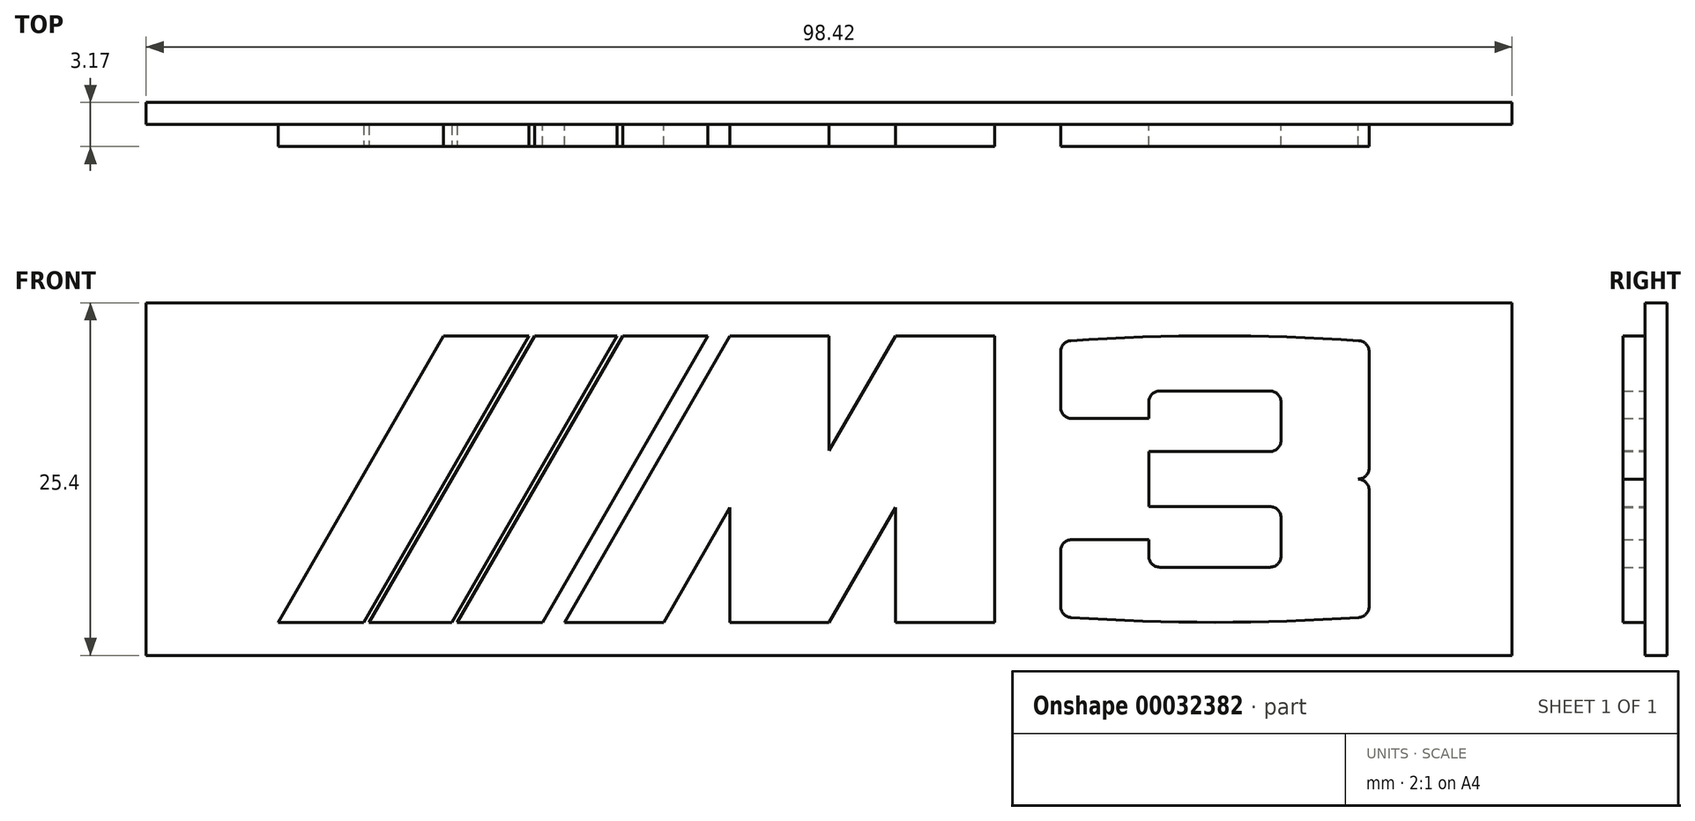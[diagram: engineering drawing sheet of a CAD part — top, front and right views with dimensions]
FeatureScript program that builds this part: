
annotation { "Feature Type Name" : "Feature", "Feature Type Description" : "" }
export const myFeature = defineFeature(function(context is Context, id is Id, definition is map)
    precondition{}
    {
        {
            var Q0;
            Q0=qCreatedBy(makeId("Front.planeOp"),FACE);
            var sketch = newSketch(context, id + "F0", { "sketchPlane" : qUnion([Q0])});
            skLineSegment(sketch, "E0.bottom", {"start": v(0, 0) * mm, "end": v(98.43, 0) * mm});
            skLineSegment(sketch, "E0.top", {"start": v(0, 25.4) * mm, "end": v(98.43, 25.4) * mm});
            skLineSegment(sketch, "E0.left", {"start": v(0, 0) * mm, "end": v(0, 25.4) * mm});
            skLineSegment(sketch, "E0.right", {"start": v(98.43, 0) * mm, "end": v(98.43, 25.4) * mm});
            skSolve(sketch);
        }
        {
            var Q0;
            Q0=makeQuery(id+"F0.imprint","IMPRINT",FACE,{"disambiguationData":[TD([[makeQuery(id+"F0.imprint","IMPRINT",EDGE,{"derivedFrom":sQuery(id+"F0.wireOp",EDGE,"E0.bottom")}),1.0]])]});
            extrude(context, id + "F1", {"entities" : qUnion([Q0]), "depth" : 1.59 * mm});
        }
        {
            var Q0;
            Q0=makeQuery(id+"F1.opExtrude","CAP_FACE",FACE,{"disambiguationData":[OSD([sQuery(id+"F0.wireOp",EDGE,"E0.bottom"),sQuery(id+"F0.wireOp",EDGE,"E0.top"),sQuery(id+"F0.wireOp",EDGE,"E0.left"),sQuery(id+"F0.wireOp",EDGE,"E0.right")])],"isStart":false});
            var sketch = newSketch(context, id + "F2", { "sketchPlane" : qUnion([Q0])});
            skLineSegment(sketch, "E1", {"start": v(0, 2.38) * mm, "end": v(98.43, 2.38) * mm, "construction": true});
            skLineSegment(sketch, "E2", {"start": v(0, 23.02) * mm, "end": v(98.43, 23.02) * mm, "construction": true});
            skLineSegment(sketch, "E3", {"start": v(9.53, 2.38) * mm, "end": v(21.44, 23.02) * mm});
            skLineSegment(sketch, "E4", {"start": v(21.44, 23.02) * mm, "end": v(40.5, 23.02) * mm});
            skLineSegment(sketch, "E5", {"start": v(40.5, 23.02) * mm, "end": v(28.58, 2.38) * mm});
            skLineSegment(sketch, "E6", {"start": v(28.58, 2.38) * mm, "end": v(9.53, 2.38) * mm});
            skLineSegment(sketch, "E7", {"start": v(30.16, 2.38) * mm, "end": v(42.08, 23.02) * mm});
            skLineSegment(sketch, "E8", {"start": v(42.08, 23.02) * mm, "end": v(49.22, 23.02) * mm});
            skLineSegment(sketch, "E9", {"start": v(49.22, 23.02) * mm, "end": v(49.22, 14.75) * mm});
            skLineSegment(sketch, "E10", {"start": v(49.22, 14.75) * mm, "end": v(54, 23.02) * mm});
            skLineSegment(sketch, "E11", {"start": v(54, 23.02) * mm, "end": v(61.14, 23.02) * mm});
            skLineSegment(sketch, "E12", {"start": v(61.14, 23.02) * mm, "end": v(61.14, 2.38) * mm});
            skLineSegment(sketch, "E13", {"start": v(61.14, 2.38) * mm, "end": v(54, 2.38) * mm});
            skLineSegment(sketch, "E14", {"start": v(54, 2.38) * mm, "end": v(54, 10.65) * mm});
            skLineSegment(sketch, "E15", {"start": v(54, 10.65) * mm, "end": v(49.22, 2.38) * mm});
            skLineSegment(sketch, "E16", {"start": v(49.22, 2.38) * mm, "end": v(42.08, 2.38) * mm});
            skLineSegment(sketch, "E17", {"start": v(42.08, 2.38) * mm, "end": v(42.08, 10.65) * mm});
            skLineSegment(sketch, "E18", {"start": v(42.08, 10.65) * mm, "end": v(37.3, 2.38) * mm});
            skLineSegment(sketch, "E19", {"start": v(37.3, 2.38) * mm, "end": v(30.16, 2.38) * mm});
            skLineSegment(sketch, "E20.left", {"start": v(65.9, 21.88) * mm, "end": v(65.9, 17.86) * mm});
            skLineSegment(sketch, "E20.right", {"start": v(88.12, 21.88) * mm, "end": v(88.12, 16.87) * mm});
            skPoint(sketch, "E21.visualSharp", {"position": v(65.9, 23.02) * mm});
            skPoint(sketch, "E22.visualSharp", {"position": v(65.9, 2.38) * mm});
            skPoint(sketch, "E23.visualSharp", {"position": v(88.12, 2.38) * mm});
            skLineSegment(sketch, "E24", {"start": v(87.33, 23.02) * mm, "end": v(87.33, 2.38) * mm, "construction": true});
            skPoint(sketch, "E25", {"position": v(87.33, 12.7) * mm});
            skArc(sketch, "E26", {"start": v(87.33, 12.7) * mm, "mid": v(87.9, 12.93) * mm, "end": v(88.12, 13.5) * mm});
            skArc(sketch, "E27", {"start": v(88.12, 11.9) * mm, "mid": v(87.9, 12.47) * mm, "end": v(87.33, 12.7) * mm});
            skLineSegment(sketch, "E28", {"start": v(65.9, 12.7) * mm, "end": v(88.12, 12.7) * mm, "construction": true});
            skLineSegment(sketch, "E29", {"start": v(66.7, 17.07) * mm, "end": v(72.25, 17.07) * mm});
            skLineSegment(sketch, "E30", {"start": v(66.7, 8.33) * mm, "end": v(72.25, 8.33) * mm});
            skLineSegment(sketch, "E31", {"start": v(72.25, 17.07) * mm, "end": v(72.25, 18.26) * mm});
            skLineSegment(sketch, "E32", {"start": v(73.04, 19.05) * mm, "end": v(80.98, 19.05) * mm});
            skLineSegment(sketch, "E33", {"start": v(81.77, 18.26) * mm, "end": v(81.77, 15.48) * mm});
            skLineSegment(sketch, "E34", {"start": v(80.98, 14.68) * mm, "end": v(72.25, 14.68) * mm});
            skLineSegment(sketch, "E35", {"start": v(72.25, 14.68) * mm, "end": v(72.25, 10.72) * mm});
            skLineSegment(sketch, "E36", {"start": v(72.25, 10.72) * mm, "end": v(80.98, 10.72) * mm});
            skLineSegment(sketch, "E37", {"start": v(81.77, 9.92) * mm, "end": v(81.77, 7.14) * mm});
            skLineSegment(sketch, "E38", {"start": v(80.98, 6.35) * mm, "end": v(73.04, 6.35) * mm});
            skLineSegment(sketch, "E39", {"start": v(72.25, 7.14) * mm, "end": v(72.25, 8.33) * mm});
            skLineSegment(sketch, "E40", {"start": v(81.77, 16.87) * mm, "end": v(88.12, 16.87) * mm, "construction": true});
            skLineSegment(sketch, "E41.trimOffspring", {"start": v(65.9, 7.54) * mm, "end": v(65.9, 3.52) * mm});
            skArc(sketch, "E42", {"start": v(66.64, 2.73) * mm, "mid": v(77.01, 2.38) * mm, "end": v(87.38, 2.73) * mm});
            skArc(sketch, "E43", {"start": v(87.38, 22.67) * mm, "mid": v(77.01, 23.02) * mm, "end": v(66.64, 22.67) * mm});
            skPoint(sketch, "E44.visualSharp", {"position": v(88.12, 22.62) * mm});
            skArc(sketch, "E44.filletArc", {"start": v(88.12, 21.88) * mm, "mid": v(87.9, 22.42) * mm, "end": v(87.38, 22.67) * mm});
            skPoint(sketch, "E45.visualSharp", {"position": v(65.9, 22.62) * mm});
            skArc(sketch, "E45.filletArc", {"start": v(66.64, 22.67) * mm, "mid": v(66.11, 22.42) * mm, "end": v(65.9, 21.88) * mm});
            skPoint(sketch, "E46.visualSharp", {"position": v(65.9, 17.07) * mm});
            skArc(sketch, "E46.filletArc", {"start": v(65.9, 17.86) * mm, "mid": v(66.13, 17.3) * mm, "end": v(66.7, 17.07) * mm});
            skPoint(sketch, "E47.visualSharp", {"position": v(65.9, 8.33) * mm});
            skArc(sketch, "E47.filletArc", {"start": v(66.7, 8.33) * mm, "mid": v(66.13, 8.1) * mm, "end": v(65.9, 7.54) * mm});
            skPoint(sketch, "E48.visualSharp", {"position": v(65.9, 2.78) * mm});
            skArc(sketch, "E48.filletArc", {"start": v(65.9, 3.52) * mm, "mid": v(66.11, 2.98) * mm, "end": v(66.64, 2.73) * mm});
            skPoint(sketch, "E49.visualSharp", {"position": v(88.12, 2.78) * mm});
            skArc(sketch, "E49.filletArc", {"start": v(87.38, 2.73) * mm, "mid": v(87.9, 2.98) * mm, "end": v(88.12, 3.52) * mm});
            skPoint(sketch, "E50.visualSharp", {"position": v(72.25, 19.05) * mm});
            skArc(sketch, "E50.filletArc", {"start": v(73.04, 19.05) * mm, "mid": v(72.48, 18.82) * mm, "end": v(72.25, 18.26) * mm});
            skPoint(sketch, "E51.visualSharp", {"position": v(81.77, 19.05) * mm});
            skArc(sketch, "E51.filletArc", {"start": v(81.77, 18.26) * mm, "mid": v(81.54, 18.82) * mm, "end": v(80.98, 19.05) * mm});
            skPoint(sketch, "E52.visualSharp", {"position": v(81.77, 14.68) * mm});
            skArc(sketch, "E52.filletArc", {"start": v(80.98, 14.68) * mm, "mid": v(81.54, 14.92) * mm, "end": v(81.77, 15.48) * mm});
            skPoint(sketch, "E53.visualSharp", {"position": v(81.77, 10.72) * mm});
            skArc(sketch, "E53.filletArc", {"start": v(81.77, 9.92) * mm, "mid": v(81.54, 10.48) * mm, "end": v(80.98, 10.72) * mm});
            skPoint(sketch, "E54.visualSharp", {"position": v(81.77, 6.35) * mm});
            skArc(sketch, "E54.filletArc", {"start": v(80.98, 6.35) * mm, "mid": v(81.54, 6.58) * mm, "end": v(81.77, 7.14) * mm});
            skPoint(sketch, "E55.visualSharp", {"position": v(72.25, 6.35) * mm});
            skArc(sketch, "E55.filletArc", {"start": v(72.25, 7.14) * mm, "mid": v(72.48, 6.58) * mm, "end": v(73.04, 6.35) * mm});
            skLineSegment(sketch, "E56", {"start": v(65.9, 12.7) * mm, "end": v(72.25, 12.7) * mm, "construction": true});
            skLineSegment(sketch, "E57.trimOffspring", {"start": v(88.12, 11.9) * mm, "end": v(88.12, 3.52) * mm});
            skLineSegment(sketch, "E58", {"start": v(88.12, 16.87) * mm, "end": v(88.12, 13.5) * mm});
            skSolve(sketch);
        }
        {
            var Q0;
            Q0 = qSketchRegion(id + "F2", true);
            extrude(context, id + "F3", {"entities" : qUnion([Q0]), "operationType" : NewBodyOperationType.ADD, "depth" : 1.59 * mm});
        }
        {
            var Q0;
            Q0=makeQuery(id+"F3.opExtrude","CAP_FACE",FACE,{"disambiguationData":[OSD([sQuery(id+"F2.wireOp",EDGE,"E3"),sQuery(id+"F2.wireOp",EDGE,"E4"),sQuery(id+"F2.wireOp",EDGE,"E5"),sQuery(id+"F2.wireOp",EDGE,"E6")])],"isStart":false});
            var sketch = newSketch(context, id + "F4", { "sketchPlane" : qUnion([Q0])});
            skLineSegment(sketch, "E59", {"start": v(27.8, 23.02) * mm, "end": v(15.88, 2.38) * mm, "construction": true});
            skLineSegment(sketch, "E60", {"start": v(34.14, 23.02) * mm, "end": v(22.23, 2.38) * mm, "construction": true});
            skLineSegment(sketch, "E61", {"start": v(15.48, 12.7) * mm, "end": v(21.83, 12.7) * mm, "construction": true});
            skLineSegment(sketch, "E62", {"start": v(21.83, 12.7) * mm, "end": v(28.18, 12.7) * mm, "construction": true});
            skLineSegment(sketch, "E63", {"start": v(28.18, 12.7) * mm, "end": v(34.53, 12.7) * mm, "construction": true});
            skLineSegment(sketch, "E64", {"start": v(34.34, 23.02) * mm, "end": v(22.42, 2.38) * mm});
            skLineSegment(sketch, "E65", {"start": v(33.94, 23.02) * mm, "end": v(22.03, 2.38) * mm});
            skLineSegment(sketch, "E66", {"start": v(33.94, 23.02) * mm, "end": v(34.34, 23.02) * mm});
            skLineSegment(sketch, "E67", {"start": v(22.03, 2.38) * mm, "end": v(22.42, 2.38) * mm});
            skLineSegment(sketch, "E68", {"start": v(27.99, 23.02) * mm, "end": v(16.07, 2.38) * mm});
            skLineSegment(sketch, "E69", {"start": v(16.07, 2.38) * mm, "end": v(15.68, 2.38) * mm});
            skLineSegment(sketch, "E70", {"start": v(15.68, 2.38) * mm, "end": v(27.6, 23.02) * mm});
            skLineSegment(sketch, "E71", {"start": v(27.6, 23.02) * mm, "end": v(27.99, 23.02) * mm});
            skSolve(sketch);
        }
        {
            var Q0;
            Q0 = qSketchRegion(id + "F4", true);
            var Q1;
            Q1=makeQuery(id+"F1.opExtrude","CAP_FACE",FACE,{"disambiguationData":[OSD([sQuery(id+"F0.wireOp",EDGE,"E0.bottom"),sQuery(id+"F0.wireOp",EDGE,"E0.top"),sQuery(id+"F0.wireOp",EDGE,"E0.left"),sQuery(id+"F0.wireOp",EDGE,"E0.right")])],"isStart":false});
            extrude(context, id + "F5", {"entities" : qUnion([Q0]), "operationType" : NewBodyOperationType.REMOVE, "endBound" : BoundingType.UP_TO_SURFACE, "oppositeDirection" : true, "endBoundEntityFace" : qUnion([Q1]), "depth" : 25.4 * mm});
        }
    });
